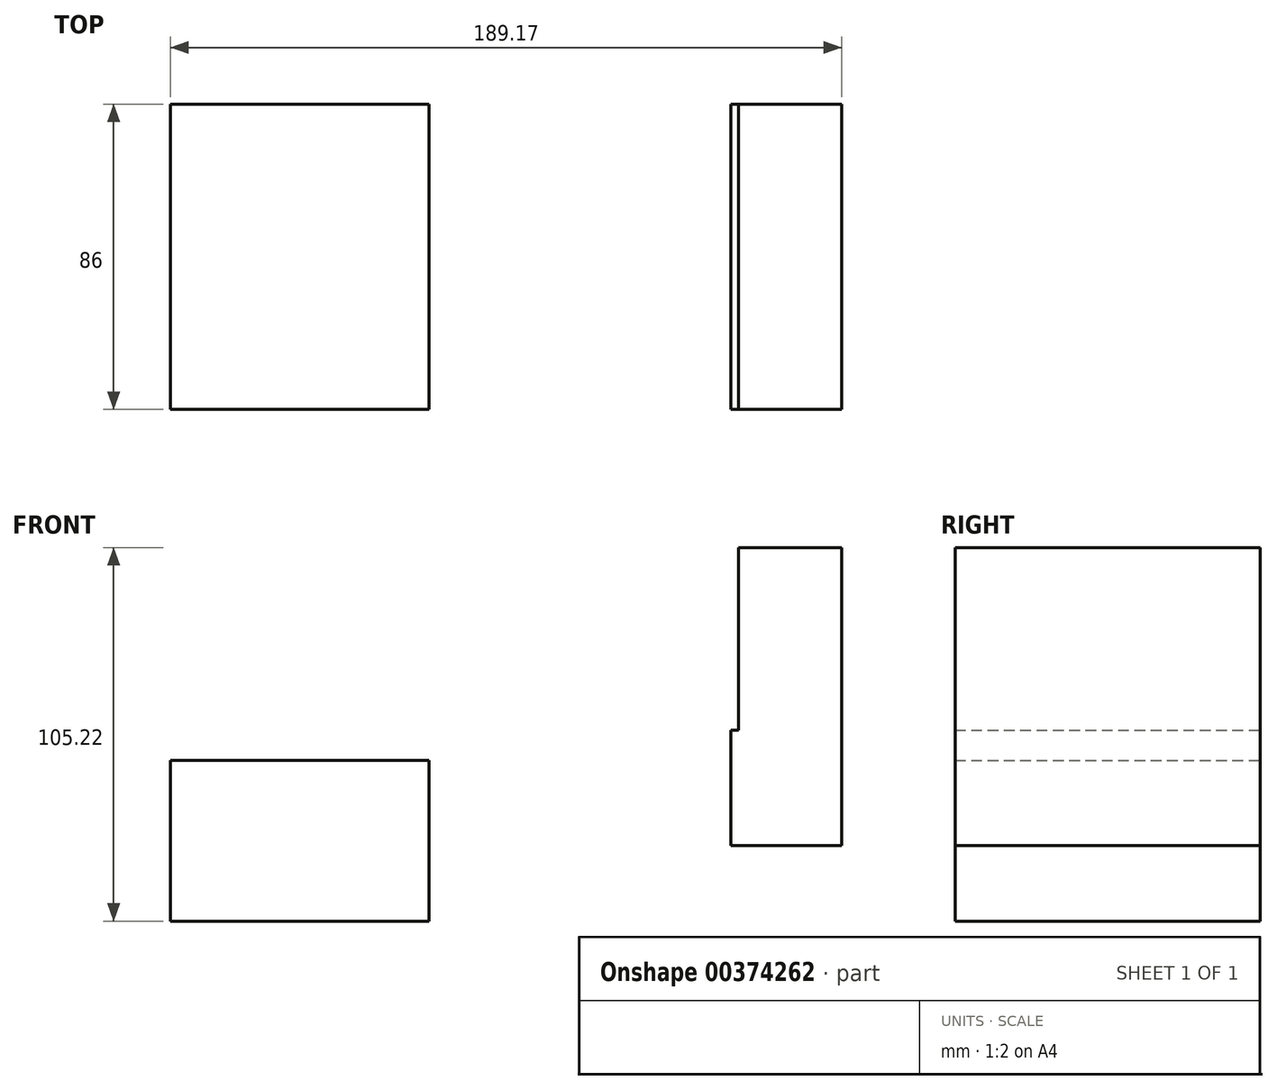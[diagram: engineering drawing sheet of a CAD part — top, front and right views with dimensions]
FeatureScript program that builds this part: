
annotation { "Feature Type Name" : "Feature", "Feature Type Description" : "" }
export const myFeature = defineFeature(function(context is Context, id is Id, definition is map)
    precondition{}
    {
        {
            var Q0;
            Q0=qCreatedBy(makeId("Front.planeOp"),FACE);
            var sketch = newSketch(context, id + "F0", { "sketchPlane" : qUnion([Q0])});
            skLineSegment(sketch, "E0.bottom", {"start": v(-61.96, 53.94) * mm, "end": v(10.97, 53.94) * mm});
            skLineSegment(sketch, "E0.top", {"start": v(-61.96, 8.65) * mm, "end": v(10.97, 8.65) * mm});
            skLineSegment(sketch, "E0.left", {"start": v(-61.96, 53.94) * mm, "end": v(-61.96, 8.65) * mm});
            skLineSegment(sketch, "E0.right", {"start": v(10.97, 53.94) * mm, "end": v(10.97, 8.65) * mm});
            skSolve(sketch);
        }
        {
            var Q0;
            Q0=qCreatedBy(makeId("Front.planeOp"),FACE);
            var sketch = newSketch(context, id + "F1", { "sketchPlane" : qUnion([Q0])});
            skLineSegment(sketch, "E1.bottom", {"start": v(95.96, 29.9) * mm, "end": v(127.21, 29.9) * mm});
            skLineSegment(sketch, "E1.top", {"start": v(95.96, 62.5) * mm, "end": v(127.21, 62.5) * mm});
            skLineSegment(sketch, "E1.left", {"start": v(95.96, 29.9) * mm, "end": v(95.96, 62.5) * mm});
            skLineSegment(sketch, "E1.right", {"start": v(127.21, 29.9) * mm, "end": v(127.21, 62.5) * mm});
            skLineSegment(sketch, "E2.bottom", {"start": v(127.21, 62.5) * mm, "end": v(98.15, 62.5) * mm});
            skLineSegment(sketch, "E2.top", {"start": v(127.21, 113.87) * mm, "end": v(98.15, 113.87) * mm});
            skLineSegment(sketch, "E2.left", {"start": v(127.21, 62.5) * mm, "end": v(127.21, 113.87) * mm});
            skLineSegment(sketch, "E2.right", {"start": v(98.15, 62.5) * mm, "end": v(98.15, 113.87) * mm});
            skSolve(sketch);
        }
        {
            var Q0;
            Q0=makeQuery(id+"F0.imprint","IMPRINT",FACE,{"disambiguationData":[TD([[makeQuery(id+"F0.imprint","IMPRINT",EDGE,{"derivedFrom":sQuery(id+"F0.wireOp",EDGE,"E0.bottom")}),-1.0]])]});
            var Q1;
            Q1 = qSketchRegion(id + "F1", true);
            extrude(context, id + "F2", {"entities" : qUnion([Q0, Q1]), "depth" : 86 * mm});
        }
    });
